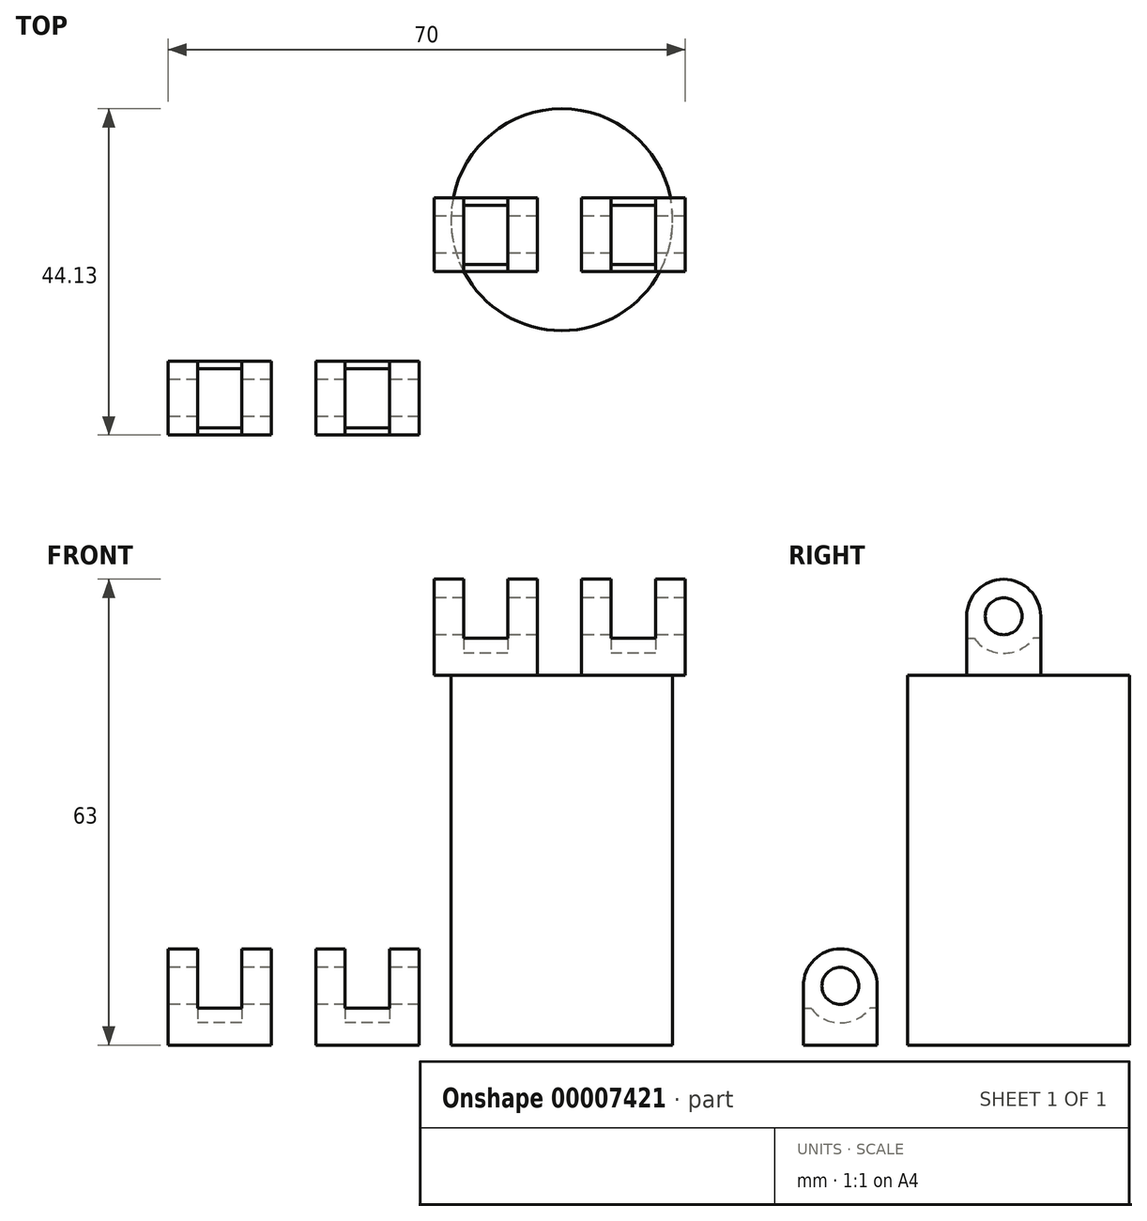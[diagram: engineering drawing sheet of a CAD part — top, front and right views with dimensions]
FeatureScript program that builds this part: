
annotation { "Feature Type Name" : "Feature", "Feature Type Description" : "" }
export const myFeature = defineFeature(function(context is Context, id is Id, definition is map)
    precondition{}
    {
        {
            var Q0;
            Q0=qCreatedBy(makeId("Top.planeOp"),FACE);
            var sketch = newSketch(context, id + "F0", { "sketchPlane" : qUnion([Q0])});
            skCircle(sketch, "E0", {"center": v(0, 0) * mm, "radius": 15 * mm});
            skSolve(sketch);
        }
        {
            var Q0;
            Q0=makeQuery(id+"F0.imprint","IMPRINT",FACE,{"disambiguationData":[TD([[makeQuery(id+"F0.imprint","IMPRINT",EDGE,{"derivedFrom":sQuery(id+"F0.wireOp",EDGE,"E0")}),1.0]])]});
            extrude(context, id + "F1", {"entities" : qUnion([Q0]), "depth" : 50 * mm});
        }
        {
            var Q0;
            Q0=qCreatedBy(makeId("Top.planeOp"),FACE);
            var sketch = newSketch(context, id + "F2", { "sketchPlane" : qUnion([Q0])});
            skLineSegment(sketch, "E1.bottom", {"start": v(-53.31, -19.13) * mm, "end": v(-49.31, -19.13) * mm});
            skLineSegment(sketch, "E1.top", {"start": v(-53.31, -29.13) * mm, "end": v(-49.31, -29.13) * mm});
            skLineSegment(sketch, "E1.left", {"start": v(-53.31, -19.13) * mm, "end": v(-53.31, -29.13) * mm});
            skLineSegment(sketch, "E1.right", {"start": v(-49.31, -19.13) * mm, "end": v(-49.31, -29.13) * mm});
            skLineSegment(sketch, "E2.bottom", {"start": v(-43.31, -19.13) * mm, "end": v(-39.31, -19.13) * mm});
            skLineSegment(sketch, "E2.top", {"start": v(-43.31, -29.13) * mm, "end": v(-39.31, -29.13) * mm});
            skLineSegment(sketch, "E2.left", {"start": v(-43.31, -19.13) * mm, "end": v(-43.31, -29.13) * mm});
            skLineSegment(sketch, "E2.right", {"start": v(-39.31, -19.13) * mm, "end": v(-39.31, -29.13) * mm});
            skSolve(sketch);
        }
        {
            var Q0;
            Q0=makeQuery(id+"F2.imprint","IMPRINT",FACE,{"disambiguationData":[TD([[makeQuery(id+"F2.imprint","IMPRINT",EDGE,{"derivedFrom":sQuery(id+"F2.wireOp",EDGE,"E1.bottom")}),-1.0]])]});
            var Q1;
            Q1=makeQuery(id+"F2.imprint","IMPRINT",FACE,{"disambiguationData":[TD([[makeQuery(id+"F2.imprint","IMPRINT",EDGE,{"derivedFrom":sQuery(id+"F2.wireOp",EDGE,"E2.bottom")}),-1.0]])]});
            extrude(context, id + "F3", {"entities" : qUnion([Q0, Q1]), "depth" : 13 * mm});
        }
        {
            var Q0;
            Q0=makeQuery(id+"F3.opExtrude","SWEPT_FACE",FACE,{"disambiguationData":[OSD([sQuery(id+"F2.wireOp",EDGE,"E2.left")])]});
            var sketch = newSketch(context, id + "F4", { "sketchPlane" : qUnion([Q0])});
            skLineSegment(sketch, "E3.bottom", {"start": v(19.13, 0) * mm, "end": v(29.13, 0) * mm});
            skLineSegment(sketch, "E3.top", {"start": v(19.13, 5) * mm, "end": v(29.13, 5) * mm});
            skLineSegment(sketch, "E3.left", {"start": v(19.13, 0) * mm, "end": v(19.13, 5) * mm});
            skLineSegment(sketch, "E3.right", {"start": v(29.13, 0) * mm, "end": v(29.13, 5) * mm});
            skSolve(sketch);
        }
        {
            var Q0;
            Q0=makeQuery(id+"F4.imprint","IMPRINT",FACE,{"disambiguationData":[TD([[makeQuery(id+"F4.imprint","IMPRINT",EDGE,{"derivedFrom":sQuery(id+"F4.wireOp",EDGE,"E3.bottom")}),1.0]])]});
            extrude(context, id + "F5", {"entities" : qUnion([Q0]), "operationType" : NewBodyOperationType.ADD, "endBound" : BoundingType.UP_TO_NEXT, "depth" : 25 * mm});
        }
        {
            var Q0;
            Q0=makeQuery(id+"F3.opExtrude","SWEPT_FACE",FACE,{"disambiguationData":[OSD([sQuery(id+"F2.wireOp",EDGE,"E1.left")])]});
            var sketch = newSketch(context, id + "F6", { "sketchPlane" : qUnion([Q0])});
            skLineSegment(sketch, "E4", {"start": v(19.13, 8) * mm, "end": v(29.13, 8) * mm, "construction": true});
            skLineSegment(sketch, "E5", {"start": v(24.13, 13) * mm, "end": v(24.13, 8) * mm, "construction": true});
            skCircle(sketch, "E6", {"center": v(24.13, 8) * mm, "radius": 5 * mm});
            skCircle(sketch, "E7", {"center": v(24.13, 8) * mm, "radius": 2.5 * mm});
            skSolve(sketch);
        }
        {
            var Q0;
            {var subQ0=sQuery(id+"F2.wireOp",EDGE,"E1.left");var subQ1=makeQuery(id+"F3.opExtrude","CAP_EDGE",EDGE,{"disambiguationData":[OSD([subQ0])],"isStart":false});var subQ2=sQuery(id+"F6.wireOp",EDGE,"E6");var subQ3=makeQuery(id+"F6.imprint","INTERSECT",VERTEX,{"derivedFrom":[subQ1,subQ2]});Q0=makeQuery(id+"F6.imprint","IMPRINT",FACE,{"disambiguationData":[TD([[makeQuery(id+"F6.imprint","IMPRINT",EDGE,{"disambiguationData":[TD([[subQ3,-1.0]])],"derivedFrom":subQ2}),-1.0]])]});}
            var Q1;
            {var subQ0=sQuery(id+"F2.wireOp",EDGE,"E1.left");var subQ1=makeQuery(id+"F3.opExtrude","CAP_EDGE",EDGE,{"disambiguationData":[OSD([subQ0])],"isStart":false});var subQ2=sQuery(id+"F6.wireOp",EDGE,"E6");var subQ3=makeQuery(id+"F6.imprint","INTERSECT",VERTEX,{"derivedFrom":[subQ1,subQ2]});Q1=makeQuery(id+"F6.imprint","IMPRINT",FACE,{"disambiguationData":[TD([[makeQuery(id+"F6.imprint","IMPRINT",EDGE,{"disambiguationData":[TD([[subQ3,1.0]])],"derivedFrom":subQ2}),-1.0]])]});}
            var Q2;
            Q2=makeQuery(id+"F6.imprint","IMPRINT",FACE,{"disambiguationData":[TD([[makeQuery(id+"F6.imprint","IMPRINT",EDGE,{"derivedFrom":sQuery(id+"F6.wireOp",EDGE,"E7")}),1.0]])]});
            extrude(context, id + "F7", {"entities" : qUnion([Q0, Q1, Q2]), "operationType" : NewBodyOperationType.REMOVE, "endBound" : BoundingType.THROUGH_ALL, "oppositeDirection" : true, "depth" : 25 * mm});
        }
        {
            var Q0;
            Q0=makeQuery(id+"F6.imprint","IMPRINT",FACE,{"disambiguationData":[TD([[makeQuery(id+"F6.imprint","IMPRINT",EDGE,{"derivedFrom":sQuery(id+"F6.wireOp",EDGE,"E7")}),-1.0]])]});
            cPlane(context, id + "F8", {"entities" : qUnion([Q0]), "cplaneType" : CPlaneType.OFFSET, "offset" : 4 * mm, "oppositeDirection" : true, "width" : 150 * mm, "height" : 150 * mm});
        }
        {
            var Q0;
            Q0=qCreatedBy(id+"F8.planeOp",FACE);
            var sketch = newSketch(context, id + "F9", { "sketchPlane" : qUnion([Q0])});
            skCircle(sketch, "E8", {"center": v(24.13, 8) * mm, "radius": 5 * mm});
            skSolve(sketch);
        }
        {
            var Q0;
            Q0=makeQuery(id+"F9.imprint","IMPRINT",FACE,{"disambiguationData":[TD([[makeQuery(id+"F9.imprint","IMPRINT",EDGE,{"derivedFrom":sQuery(id+"F9.wireOp",EDGE,"E8")}),1.0]])]});
            extrude(context, id + "F10", {"entities" : qUnion([Q0]), "operationType" : NewBodyOperationType.REMOVE, "oppositeDirection" : true, "depth" : 6 * mm});
        }
        {
            var Q0;
            Q0=makeQuery(id+"F3.opExtrude","SWEPT_BODY",BODY,{"disambiguationData":[OSD([sQuery(id+"F2.wireOp",EDGE,"E1.bottom"),sQuery(id+"F2.wireOp",EDGE,"E1.top"),sQuery(id+"F2.wireOp",EDGE,"E1.left"),sQuery(id+"F2.wireOp",EDGE,"E1.right")])]});
            transform(context, id + "F11", {"entities" : qUnion([Q0]), "transformType" : TransformType.TRANSLATION_3D, "dx" : 20 * mm, "dy" : 0 * mm, "dz" : 0 * mm, "makeCopy" : true});
        }
        {
            var Q0;
            Q0=makeQuery(id+"F3.opExtrude","SWEPT_BODY",BODY,{"disambiguationData":[OSD([sQuery(id+"F2.wireOp",EDGE,"E1.bottom"),sQuery(id+"F2.wireOp",EDGE,"E1.top"),sQuery(id+"F2.wireOp",EDGE,"E1.left"),sQuery(id+"F2.wireOp",EDGE,"E1.right")])]});
            var Q1;
            Q1=makeQuery(id+"F11.opPattern","COPY",BODY,{"derivedFrom":makeQuery(id+"F3.opExtrude","SWEPT_BODY",BODY,{"disambiguationData":[OSD([sQuery(id+"F2.wireOp",EDGE,"E1.bottom"),sQuery(id+"F2.wireOp",EDGE,"E1.top"),sQuery(id+"F2.wireOp",EDGE,"E1.left"),sQuery(id+"F2.wireOp",EDGE,"E1.right")])]}),"instanceName":"1"});
            transform(context, id + "F12", {"entities" : qUnion([Q0, Q1]), "transformType" : TransformType.TRANSLATION_3D, "dx" : 36 * mm, "dy" : 22.1 * mm, "dz" : 50 * mm, "makeCopy" : true});
        }
    });
